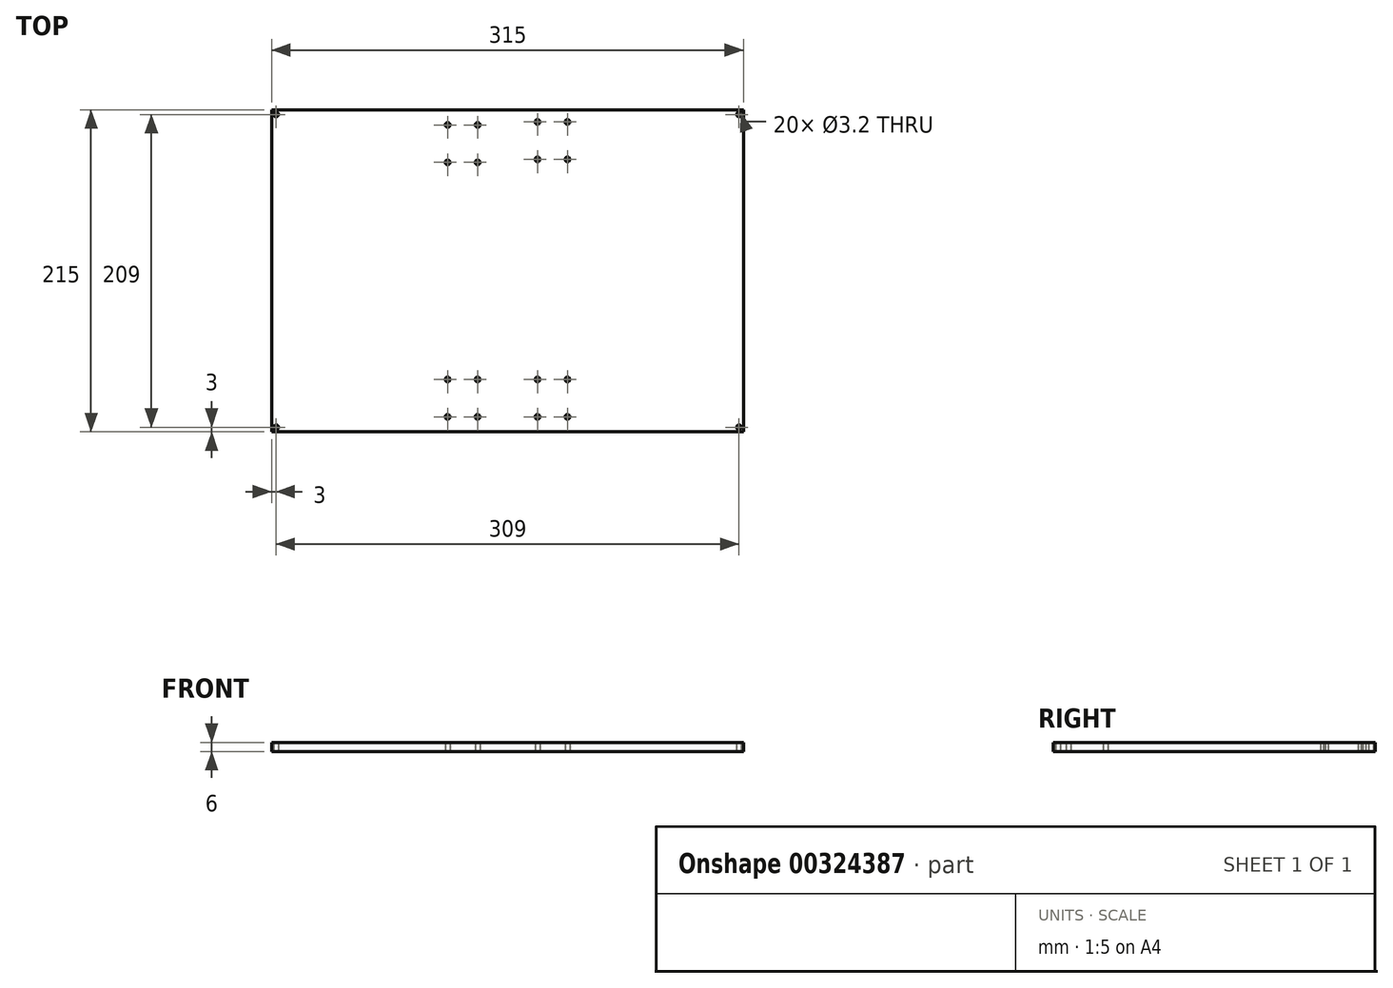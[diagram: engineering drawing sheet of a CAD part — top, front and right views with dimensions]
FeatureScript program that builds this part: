
annotation { "Feature Type Name" : "Feature", "Feature Type Description" : "" }
export const myFeature = defineFeature(function(context is Context, id is Id, definition is map)
    precondition{}
    {
        {
            var Q0;
            Q0=qCreatedBy(makeId("Top.planeOp"),FACE);
            var sketch = newSketch(context, id + "F0", { "sketchPlane" : qUnion([Q0])});
            skLineSegment(sketch, "E0.bottom", {"start": v(157.5, 107.5) * mm, "end": v(-157.5, 107.5) * mm});
            skLineSegment(sketch, "E0.top", {"start": v(157.5, -107.5) * mm, "end": v(-157.5, -107.5) * mm});
            skLineSegment(sketch, "E0.left", {"start": v(157.5, 107.5) * mm, "end": v(157.5, -107.5) * mm});
            skLineSegment(sketch, "E0.right", {"start": v(-157.5, 107.5) * mm, "end": v(-157.5, -107.5) * mm});
            skPoint(sketch, "E0.middle", {"position": v(0, 0) * mm});
            skCircle(sketch, "E1", {"center": v(-154.5, 104.5) * mm, "radius": 1.6 * mm});
            skCircle(sketch, "E2", {"center": v(154.5, 104.5) * mm, "radius": 1.6 * mm});
            skCircle(sketch, "E3", {"center": v(154.5, -104.5) * mm, "radius": 1.6 * mm});
            skCircle(sketch, "E4", {"center": v(-154.5, -104.5) * mm, "radius": 1.6 * mm});
            skPoint(sketch, "E5", {"position": v(0, 107.5) * mm});
            skLineSegment(sketch, "E6", {"start": v(0, 141.01) * mm, "end": v(0, -143.13) * mm, "construction": true});
            skLineSegment(sketch, "E7", {"start": v(248.7, 0) * mm, "end": v(-277.09, 0) * mm, "construction": true});
            skPoint(sketch, "E7.endSnap0", {"position": v(157.5, 0) * mm});
            skLineSegment(sketch, "E8", {"start": v(248.7, -85) * mm, "end": v(-291.76, -85) * mm, "construction": true});
            skLineSegment(sketch, "E9", {"start": v(-277.09, 85) * mm, "end": v(253.93, 85) * mm, "construction": true});
            skCircle(sketch, "E10", {"center": v(-40, 97.5) * mm, "radius": 1.6 * mm});
            skCircle(sketch, "E11", {"center": v(-20, 97.5) * mm, "radius": 1.6 * mm});
            skCircle(sketch, "E12", {"center": v(-40, 72.5) * mm, "radius": 1.6 * mm});
            skCircle(sketch, "E13", {"center": v(-20, 72.5) * mm, "radius": 1.6 * mm});
            skCircle(sketch, "E14", {"center": v(20, 99.5) * mm, "radius": 1.6 * mm});
            skCircle(sketch, "E15", {"center": v(40, 99.5) * mm, "radius": 1.6 * mm});
            skCircle(sketch, "E16", {"center": v(20, 74.5) * mm, "radius": 1.6 * mm});
            skCircle(sketch, "E17", {"center": v(40, 74.5) * mm, "radius": 1.6 * mm});
            skCircle(sketch, "E18", {"center": v(-40, -72.5) * mm, "radius": 1.6 * mm});
            skCircle(sketch, "E19", {"center": v(-20, -72.5) * mm, "radius": 1.6 * mm});
            skCircle(sketch, "E20", {"center": v(-40, -97.5) * mm, "radius": 1.6 * mm});
            skCircle(sketch, "E21", {"center": v(-20, -97.5) * mm, "radius": 1.6 * mm});
            skCircle(sketch, "E22", {"center": v(20, -72.5) * mm, "radius": 1.6 * mm});
            skCircle(sketch, "E23", {"center": v(40, -72.5) * mm, "radius": 1.6 * mm});
            skCircle(sketch, "E24", {"center": v(20, -97.5) * mm, "radius": 1.6 * mm});
            skCircle(sketch, "E25", {"center": v(40, -97.5) * mm, "radius": 1.6 * mm});
            skSolve(sketch);
        }
        {
            var Q0;
            Q0=makeQuery(id+"F0.imprint","IMPRINT",FACE,{"disambiguationData":[TD([[makeQuery(id+"F0.imprint","IMPRINT",EDGE,{"derivedFrom":sQuery(id+"F0.wireOp",EDGE,"E0.bottom")}),1.0]])]});
            extrude(context, id + "F1", {"entities" : qUnion([Q0]), "depth" : 6 * mm});
        }
    });
